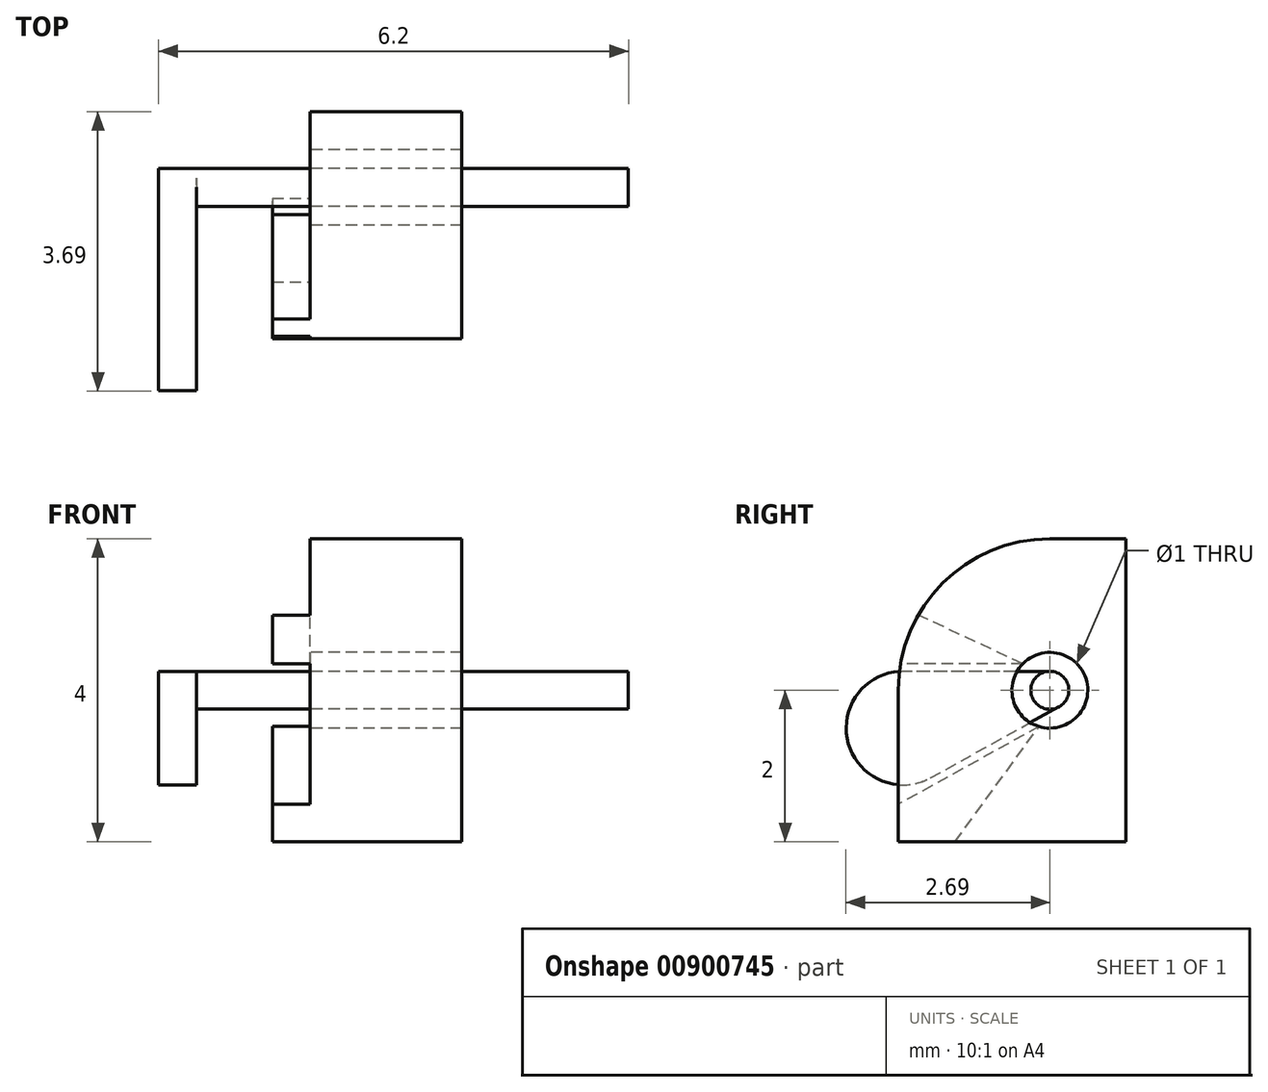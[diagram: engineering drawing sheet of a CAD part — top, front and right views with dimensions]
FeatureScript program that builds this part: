
annotation { "Feature Type Name" : "Feature", "Feature Type Description" : "" }
export const myFeature = defineFeature(function(context is Context, id is Id, definition is map)
    precondition{}
    {
        {
            var Q0;
            Q0=qCreatedBy(makeId("Top.planeOp"),FACE);
            var sketch = newSketch(context, id + "F0", { "sketchPlane" : qUnion([Q0])});
            skLineSegment(sketch, "E0.bottom", {"start": v(1, 1.5) * mm, "end": v(-1, 1.5) * mm});
            skLineSegment(sketch, "E0.top", {"start": v(1, -1.5) * mm, "end": v(-1, -1.5) * mm});
            skLineSegment(sketch, "E0.left", {"start": v(1, 1.5) * mm, "end": v(1, -1.5) * mm});
            skLineSegment(sketch, "E0.right", {"start": v(-1, 1.5) * mm, "end": v(-1, -1.5) * mm});
            skPoint(sketch, "E0.middle", {"position": v(0, 0) * mm});
            skSolve(sketch);
        }
        {
            var Q0;
            Q0 = qSketchRegion(id + "F0", true);
            extrude(context, id + "F1", {"entities" : qUnion([Q0]), "depth" : 4 * mm, "offsetDistance" : 25.4 * mm});
        }
        {
            var Q0;
            Q0=makeQuery(id+"F1.opExtrude","CAP_EDGE",EDGE,{"disambiguationData":[OSD([sQuery(id+"F0.wireOp",EDGE,"E0.top")])],"isStart":false});
            fillet(context, id + "F2", {"entities" : qUnion([Q0]), "radius" : 2 * mm, "tangentPropagation" : true, "allowEdgeOverflow" : false});
        }
        {
            var Q0;
            Q0=makeQuery(id+"F1.opExtrude","SWEPT_FACE",FACE,{"disambiguationData":[OSD([sQuery(id+"F0.wireOp",EDGE,"E0.right")])]});
            var sketch = newSketch(context, id + "F3", { "sketchPlane" : qUnion([Q0])});
            skCircle(sketch, "E1", {"center": v(-0.5, 2) * mm, "radius": 0.5 * mm});
            skSolve(sketch);
        }
        {
            var Q0;
            Q0 = qSketchRegion(id + "F3", true);
            extrude(context, id + "F4", {"entities" : qUnion([Q0]), "operationType" : NewBodyOperationType.REMOVE, "endBound" : BoundingType.THROUGH_ALL, "oppositeDirection" : true, "depth" : 25.4 * mm, "offsetDistance" : 25.4 * mm});
        }
        {
            var Q0;
            Q0=makeQuery(id+"F1.opExtrude","SWEPT_FACE",FACE,{"disambiguationData":[OSD([sQuery(id+"F0.wireOp",EDGE,"E0.right")])]});
            cPlane(context, id + "F5", {"entities" : qUnion([Q0]), "cplaneType" : CPlaneType.OFFSET, "offset" : 2 * mm, "width" : 152.4 * mm, "height" : 152.4 * mm});
        }
        {
            var Q0;
            Q0=qCreatedBy(id+"F5.planeOp",FACE);
            var sketch = newSketch(context, id + "F6", { "sketchPlane" : qUnion([Q0])});
            skCircle(sketch, "E2", {"center": v(-0.5, 2) * mm, "radius": 0.25 * mm});
            skSolve(sketch);
        }
        {
            var Q0;
            Q0 = qSketchRegion(id + "F6", true);
            extrude(context, id + "F7", {"entities" : qUnion([Q0]), "oppositeDirection" : true, "depth" : 6.2 * mm, "offsetDistance" : 25.4 * mm});
        }
        {
            var Q0;
            Q0=makeQuery(id+"F7.opExtrude","CAP_FACE",FACE,{"disambiguationData":[OSD([sQuery(id+"F6.wireOp",EDGE,"E2")])],"isStart":true});
            var sketch = newSketch(context, id + "F8", { "sketchPlane" : qUnion([Q0])});
            skCircle(sketch, "E3.0", {"center": v(-0.5, 2) * mm, "radius": 0.25 * mm});
            skLineSegment(sketch, "E4", {"start": v(-0.5, 2.25) * mm, "end": v(1.44, 2.25) * mm});
            skCircle(sketch, "E5", {"center": v(1.44, 1.5) * mm, "radius": 0.75 * mm});
            skLineSegment(sketch, "E6", {"start": v(1.07, 0.84) * mm, "end": v(-0.62, 1.78) * mm});
            skSolve(sketch);
        }
        {
            var Q0;
            Q0 = qSketchRegion(id + "F8", true);
            extrude(context, id + "F9", {"entities" : qUnion([Q0]), "operationType" : NewBodyOperationType.ADD, "oppositeDirection" : true, "depth" : 0.5 * mm, "offsetDistance" : 25.4 * mm});
        }
        {
            var Q0;
            Q0=makeQuery(id+"F1.opExtrude","SWEPT_FACE",FACE,{"disambiguationData":[OSD([sQuery(id+"F0.wireOp",EDGE,"E0.right")])]});
            var sketch = newSketch(context, id + "F10", { "sketchPlane" : qUnion([Q0])});
            skLineSegment(sketch, "E7", {"start": v(-0.14, 2.35) * mm, "end": v(1.47, 2.35) * mm});
            skArc(sketch, "E8.0", {"start": v(1.5, 2) * mm, "mid": v(0.91, 3.41) * mm, "end": v(-0.5, 4) * mm});
            skCircle(sketch, "E8.1", {"center": v(-0.5, 2) * mm, "radius": 0.5 * mm});
            skLineSegment(sketch, "E9", {"start": v(-0.14, 2.35) * mm, "end": v(1.24, 3) * mm});
            skLineSegment(sketch, "E10", {"start": v(-0.36, 1.52) * mm, "end": v(1.5, 0.5) * mm});
            skLineSegment(sketch, "E11", {"start": v(1.5, 0.5) * mm, "end": v(1.5, 0) * mm});
            skLineSegment(sketch, "E12", {"start": v(1.5, 0) * mm, "end": v(0.75, 0) * mm});
            skLineSegment(sketch, "E13", {"start": v(0.75, 0) * mm, "end": v(-0.36, 1.52) * mm});
            skSolve(sketch);
        }
        {
            var Q0;
            {var subQ0=sQuery(id+"F10.wireOp",EDGE,"E7");Q0=makeQuery(id+"F10.imprint","IMPRINT",FACE,{"disambiguationData":[TD([[makeQuery(id+"F10.imprint","IMPRINT",EDGE,{"derivedFrom":subQ0}),1.0]])]});}
            var Q1;
            Q1=makeQuery(id+"F10.imprint","IMPRINT",FACE,{"disambiguationData":[TD([[makeQuery(id+"F10.imprint","IMPRINT",EDGE,{"derivedFrom":sQuery(id+"F10.wireOp",EDGE,"E10")}),-1.0]])]});
            extrude(context, id + "F11", {"entities" : qUnion([Q0, Q1]), "operationType" : NewBodyOperationType.ADD, "depth" : 0.5 * mm, "offsetDistance" : 25.4 * mm});
        }
    });
